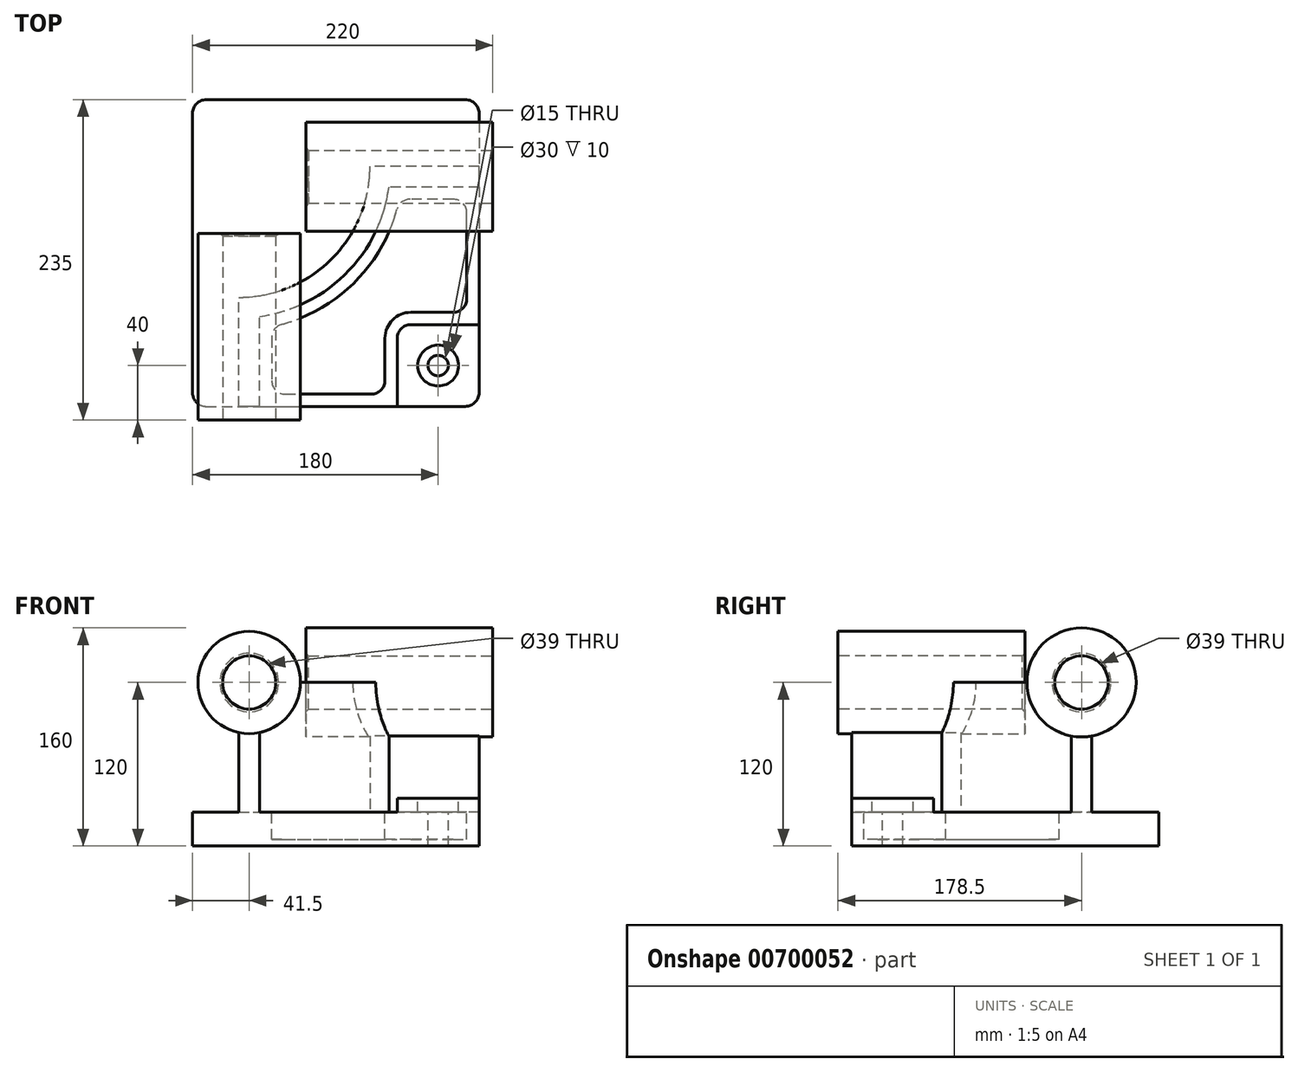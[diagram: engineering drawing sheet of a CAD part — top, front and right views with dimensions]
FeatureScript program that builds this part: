
annotation { "Feature Type Name" : "Feature", "Feature Type Description" : "" }
export const myFeature = defineFeature(function(context is Context, id is Id, definition is map)
    precondition{}
    {
        {
            var Q0;
            Q0=qCreatedBy(makeId("Top.planeOp"),FACE);
            var sketch = newSketch(context, id + "F0", { "sketchPlane" : qUnion([Q0])});
            skLineSegment(sketch, "E0.bottom", {"start": v(-105, 112.5) * mm, "end": v(105, 112.5) * mm});
            skLineSegment(sketch, "E0.top", {"start": v(-105, -112.5) * mm, "end": v(105, -112.5) * mm});
            skLineSegment(sketch, "E0.left", {"start": v(-105, 112.5) * mm, "end": v(-105, -112.5) * mm});
            skLineSegment(sketch, "E0.right", {"start": v(105, 112.5) * mm, "end": v(105, -112.5) * mm});
            skPoint(sketch, "E0.middle", {"position": v(0, 0) * mm});
            skSolve(sketch);
        }
        {
            var Q0;
            Q0=makeQuery(id+"F0.imprint","IMPRINT",FACE,{"disambiguationData":[TD([[makeQuery(id+"F0.imprint","IMPRINT",EDGE,{"derivedFrom":sQuery(id+"F0.wireOp",EDGE,"E0.bottom")}),-1.0]])]});
            extrude(context, id + "F1", {"entities" : qUnion([Q0]), "depth" : 25 * mm, "offsetDistance" : 25.4 * mm});
        }
        {
            var Q0;
            Q0=makeQuery(id+"F1.opExtrude","CAP_FACE",FACE,{"disambiguationData":[OSD([sQuery(id+"F0.wireOp",EDGE,"E0.bottom"),sQuery(id+"F0.wireOp",EDGE,"E0.top"),sQuery(id+"F0.wireOp",EDGE,"E0.left"),sQuery(id+"F0.wireOp",EDGE,"E0.right")])],"isStart":false});
            var sketch = newSketch(context, id + "F2", { "sketchPlane" : qUnion([Q0])});
            skLineSegment(sketch, "E1", {"start": v(-71, -112.5) * mm, "end": v(-71, -32.5) * mm});
            skLineSegment(sketch, "E2", {"start": v(105, 63.5) * mm, "end": v(25, 63.5) * mm});
            skArc(sketch, "E3", {"start": v(-71, -32.5) * mm, "mid": v(-3.12, -4.38) * mm, "end": v(25, 63.5) * mm});
            skLineSegment(sketch, "E4", {"start": v(-71, 63.5) * mm, "end": v(25, 63.5) * mm, "construction": true});
            skLineSegment(sketch, "E5", {"start": v(-71, 63.5) * mm, "end": v(-71, -32.5) * mm, "construction": true});
            skLineSegment(sketch, "E6.0", {"start": v(-56, -112.5) * mm, "end": v(-56, -46.48) * mm});
            skArc(sketch, "E6.1", {"start": v(-56, -46.48) * mm, "mid": v(7.49, -14.99) * mm, "end": v(38.98, 48.5) * mm});
            skLineSegment(sketch, "E6.2", {"start": v(105, 48.5) * mm, "end": v(38.98, 48.5) * mm});
            skLineSegment(sketch, "E7.0", {"start": v(105, 112.5) * mm, "end": v(105, -112.5) * mm});
            skLineSegment(sketch, "E8.0", {"start": v(-105, -112.5) * mm, "end": v(105, -112.5) * mm});
            skSolve(sketch);
        }
        {
            var Q0;
            {var subQ2=sQuery(id+"F2.wireOp",EDGE,"E1");Q0=makeQuery(id+"F2.imprint","IMPRINT",FACE,{"disambiguationData":[TD([[makeQuery(id+"F2.imprint","IMPRINT",EDGE,{"derivedFrom":subQ2}),-1.0]])]});}
            extrude(context, id + "F3", {"entities" : qUnion([Q0]), "operationType" : NewBodyOperationType.ADD, "depth" : 95 * mm, "offsetDistance" : 25.4 * mm});
        }
        {
            var Q0;
            Q0=makeQuery(id+"F3.boolean.opBoolean","MERGE",FACE,{"derivedFrom":[makeQuery(id+"F1.opExtrude","SWEPT_FACE",FACE,{"disambiguationData":[OSD([sQuery(id+"F0.wireOp",EDGE,"E0.top")])]}),makeQuery(id+"F3.opExtrude","SWEPT_FACE",FACE,{"disambiguationData":[OSD([sQuery(id+"F2.wireOp",EDGE,"E8.0")])]})]});
            var sketch = newSketch(context, id + "F4", { "sketchPlane" : qUnion([Q0])});
            skCircle(sketch, "E9", {"center": v(-63.5, 120) * mm, "radius": 37.5 * mm});
            skSolve(sketch);
        }
        {
            var Q0;
            Q0 = qSketchRegion(id + "F4", true);
            extrude(context, id + "F5", {"entities" : qUnion([Q0]), "operationType" : NewBodyOperationType.ADD, "depth" : 10 * mm, "offsetDistance" : 25.4 * mm, "hasSecondDirection" : true, "secondDirectionOppositeDirection" : true, "secondDirectionDepth" : 127 * mm});
        }
        {
            var Q0;
            Q0=makeQuery(id+"F3.boolean.opBoolean","MERGE",FACE,{"derivedFrom":[makeQuery(id+"F1.opExtrude","SWEPT_FACE",FACE,{"disambiguationData":[OSD([sQuery(id+"F0.wireOp",EDGE,"E0.right")])]}),makeQuery(id+"F3.opExtrude","SWEPT_FACE",FACE,{"disambiguationData":[OSD([sQuery(id+"F2.wireOp",EDGE,"E7.0")])]})]});
            var sketch = newSketch(context, id + "F6", { "sketchPlane" : qUnion([Q0])});
            skCircle(sketch, "E10", {"center": v(56, 120) * mm, "radius": 40 * mm});
            skSolve(sketch);
        }
        {
            var Q0;
            Q0 = qSketchRegion(id + "F6", true);
            extrude(context, id + "F7", {"entities" : qUnion([Q0]), "operationType" : NewBodyOperationType.ADD, "depth" : 10 * mm, "offsetDistance" : 25.4 * mm, "hasSecondDirection" : true, "secondDirectionOppositeDirection" : true, "secondDirectionDepth" : 127 * mm});
        }
        {
            var Q0;
            {var subQ0=sQuery(id+"F0.wireOp",EDGE,"E0.right");var subQ1=sQuery(id+"F0.wireOp",EDGE,"E0.top");Q0=makeQuery(id+"F3.boolean.opBoolean","SPLIT",FACE,{"disambiguationData":[TD([makeQuery(id+"F3.opExtrude","SWEPT_FACE",FACE,{"disambiguationData":[OSD([sQuery(id+"F2.wireOp",EDGE,"E6.0")])]})])],"derivedFrom":makeQuery(id+"F1.opExtrude","CAP_FACE",FACE,{"disambiguationData":[OSD([sQuery(id+"F0.wireOp",EDGE,"E0.bottom"),subQ1,sQuery(id+"F0.wireOp",EDGE,"E0.left"),subQ0])],"isStart":false})});}
            var sketch = newSketch(context, id + "F8", { "sketchPlane" : qUnion([Q0])});
            skLineSegment(sketch, "E11.bottom", {"start": v(105, -112.5) * mm, "end": v(45, -112.5) * mm});
            skLineSegment(sketch, "E11.top", {"start": v(105, -52.5) * mm, "end": v(45, -52.5) * mm});
            skLineSegment(sketch, "E11.left", {"start": v(105, -112.5) * mm, "end": v(105, -52.5) * mm});
            skLineSegment(sketch, "E11.right", {"start": v(45, -112.5) * mm, "end": v(45, -52.5) * mm});
            skSolve(sketch);
        }
        {
            var Q0;
            Q0 = qSketchRegion(id + "F8", true);
            extrude(context, id + "F9", {"entities" : qUnion([Q0]), "operationType" : NewBodyOperationType.ADD, "depth" : 10 * mm, "offsetDistance" : 25.4 * mm});
        }
        {
            var Q0;
            Q0=makeQuery(id+"F9.opExtrude","SWEPT_EDGE",EDGE,{"disambiguationData":[OSD([sQuery(id+"F8.wireOp",EDGE,"E11.top"),sQuery(id+"F8.wireOp",EDGE,"E11.right")])]});
            fillet(context, id + "F10", {"entities" : qUnion([Q0]), "radius" : 10 * mm, "tangentPropagation" : true, "allowEdgeOverflow" : false});
        }
        {
            var Q0;
            {var subQ0=sQuery(id+"F0.wireOp",EDGE,"E0.right");var subQ1=sQuery(id+"F0.wireOp",EDGE,"E0.top");Q0=makeQuery(id+"F3.boolean.opBoolean","SPLIT",FACE,{"disambiguationData":[TD([makeQuery(id+"F3.opExtrude","SWEPT_FACE",FACE,{"disambiguationData":[OSD([sQuery(id+"F2.wireOp",EDGE,"E6.0")])]})])],"derivedFrom":makeQuery(id+"F1.opExtrude","CAP_FACE",FACE,{"disambiguationData":[OSD([sQuery(id+"F0.wireOp",EDGE,"E0.bottom"),subQ1,sQuery(id+"F0.wireOp",EDGE,"E0.left"),subQ0])],"isStart":false})});}
            var sketch = newSketch(context, id + "F11", { "sketchPlane" : qUnion([Q0])});
            skLineSegment(sketch, "E12.0", {"start": v(-47, -54.08) * mm, "end": v(-47, -103.5) * mm});
            skArc(sketch, "E12.1", {"start": v(46.58, 39.5) * mm, "mid": v(13.85, -21.35) * mm, "end": v(-47, -54.08) * mm});
            skLineSegment(sketch, "E12.2", {"start": v(-47, -103.5) * mm, "end": v(36, -103.5) * mm});
            skLineSegment(sketch, "E12.3", {"start": v(96, 39.5) * mm, "end": v(46.58, 39.5) * mm});
            skLineSegment(sketch, "E12.4", {"start": v(36, -103.5) * mm, "end": v(36, -62.5) * mm});
            skArc(sketch, "E12.5", {"start": v(36, -62.5) * mm, "mid": v(41.56, -49.06) * mm, "end": v(55, -43.5) * mm});
            skLineSegment(sketch, "E12.6", {"start": v(55, -43.5) * mm, "end": v(96, -43.5) * mm});
            skLineSegment(sketch, "E12.7", {"start": v(96, -43.5) * mm, "end": v(96, 39.5) * mm});
            skSolve(sketch);
        }
        {
            var Q0;
            Q0=makeQuery(id+"F11.imprint","IMPRINT",FACE,{"disambiguationData":[TD([[makeQuery(id+"F11.imprint","IMPRINT",EDGE,{"derivedFrom":sQuery(id+"F11.wireOp",EDGE,"E12.0")}),1.0]])]});
            extrude(context, id + "F12", {"entities" : qUnion([Q0]), "operationType" : NewBodyOperationType.REMOVE, "oppositeDirection" : true, "depth" : 20 * mm, "offsetDistance" : 25.4 * mm});
        }
        {
            var Q0;
            Q0=makeQuery(id+"F9.opExtrude","CAP_FACE",FACE,{"disambiguationData":[OSD([sQuery(id+"F8.wireOp",EDGE,"E11.bottom"),sQuery(id+"F8.wireOp",EDGE,"E11.top"),sQuery(id+"F8.wireOp",EDGE,"E11.left"),sQuery(id+"F8.wireOp",EDGE,"E11.right")])],"isStart":false});
            var sketch = newSketch(context, id + "F13", { "sketchPlane" : qUnion([Q0])});
            skCircle(sketch, "E13", {"center": v(75, -82.5) * mm, "radius": 15 * mm});
            skSolve(sketch);
        }
        {
            var Q0;
            Q0=sQuery(id+"F13.wireOp",VERTEX,"E13.center");
            var Q1;
            Q1=makeQuery(id+"F1.opExtrude","SWEPT_BODY",BODY,{"disambiguationData":[OSD([sQuery(id+"F0.wireOp",EDGE,"E0.bottom"),sQuery(id+"F0.wireOp",EDGE,"E0.top"),sQuery(id+"F0.wireOp",EDGE,"E0.left"),sQuery(id+"F0.wireOp",EDGE,"E0.right")])]});
            hole(context, id + "F14", {"style" : HoleStyle.C_BORE, "endStyle" : HoleEndStyle.THROUGH, "holeDiameter" : 15 * mm, "cBoreDiameter" : 30 * mm, "cBoreDepth" : 10 * mm, "majorDiameter" : 6.35 * mm, "isTappedThrough" : true, "tappedDepth" : 12.7 * mm, "tapClearance" : 3, "locations" : qUnion([Q0]), "scope" : qUnion([Q1])});
        }
        {
            var Q0;
            Q0=makeQuery(id+"F12.boolean.opBoolean","COPY",EDGE,{"derivedFrom":makeQuery(id+"F12.opExtrude","SWEPT_EDGE",EDGE,{"disambiguationData":[OSD([sQuery(id+"F11.wireOp",EDGE,"E12.0"),sQuery(id+"F11.wireOp",EDGE,"E12.1")])]})});
            var Q1;
            Q1=makeQuery(id+"F12.boolean.opBoolean","COPY",EDGE,{"derivedFrom":makeQuery(id+"F12.opExtrude","SWEPT_EDGE",EDGE,{"disambiguationData":[OSD([sQuery(id+"F11.wireOp",EDGE,"E12.1"),sQuery(id+"F11.wireOp",EDGE,"E12.3")])]})});
            var Q2;
            Q2=makeQuery(id+"F12.boolean.opBoolean","COPY",EDGE,{"derivedFrom":makeQuery(id+"F12.opExtrude","SWEPT_EDGE",EDGE,{"disambiguationData":[OSD([sQuery(id+"F11.wireOp",EDGE,"E12.3"),sQuery(id+"F11.wireOp",EDGE,"E12.7")])]})});
            var Q3;
            Q3=makeQuery(id+"F12.boolean.opBoolean","COPY",EDGE,{"derivedFrom":makeQuery(id+"F12.opExtrude","SWEPT_EDGE",EDGE,{"disambiguationData":[OSD([sQuery(id+"F11.wireOp",EDGE,"E12.6"),sQuery(id+"F11.wireOp",EDGE,"E12.7")])]})});
            var Q4;
            Q4=makeQuery(id+"F12.boolean.opBoolean","COPY",EDGE,{"derivedFrom":makeQuery(id+"F12.opExtrude","SWEPT_EDGE",EDGE,{"disambiguationData":[OSD([sQuery(id+"F11.wireOp",EDGE,"E12.2"),sQuery(id+"F11.wireOp",EDGE,"E12.4")])]})});
            var Q5;
            Q5=makeQuery(id+"F12.boolean.opBoolean","COPY",EDGE,{"derivedFrom":makeQuery(id+"F12.opExtrude","SWEPT_EDGE",EDGE,{"disambiguationData":[OSD([sQuery(id+"F11.wireOp",EDGE,"E12.0"),sQuery(id+"F11.wireOp",EDGE,"E12.2")])]})});
            fillet(context, id + "F15", {"entities" : qUnion([Q0, Q1, Q2, Q3, Q4, Q5]), "radius" : 10 * mm, "tangentPropagation" : true, "allowEdgeOverflow" : false});
        }
        {
            var Q0;
            Q0=makeQuery(id+"F5.opExtrude","CAP_FACE",FACE,{"disambiguationData":[OSD([sQuery(id+"F4.wireOp",EDGE,"E9")])],"isStart":false});
            var sketch = newSketch(context, id + "F16", { "sketchPlane" : qUnion([Q0])});
            skCircle(sketch, "E14", {"center": v(-63.5, 120) * mm, "radius": 19.5 * mm});
            skSolve(sketch);
        }
        {
            var Q0;
            Q0 = qSketchRegion(id + "F16", true);
            extrude(context, id + "F17", {"entities" : qUnion([Q0]), "operationType" : NewBodyOperationType.REMOVE, "endBound" : BoundingType.THROUGH_ALL, "oppositeDirection" : true, "depth" : 25.4 * mm, "offsetDistance" : 25.4 * mm});
        }
        {
            var Q0;
            Q0=makeQuery(id+"F7.opExtrude","CAP_FACE",FACE,{"disambiguationData":[OSD([sQuery(id+"F6.wireOp",EDGE,"E10")])],"isStart":false});
            var sketch = newSketch(context, id + "F18", { "sketchPlane" : qUnion([Q0])});
            skCircle(sketch, "E15", {"center": v(56, 120) * mm, "radius": 19.5 * mm});
            skSolve(sketch);
        }
        {
            var Q0;
            Q0 = qSketchRegion(id + "F18", true);
            extrude(context, id + "F19", {"entities" : qUnion([Q0]), "operationType" : NewBodyOperationType.REMOVE, "endBound" : BoundingType.THROUGH_ALL, "oppositeDirection" : true, "depth" : 25.4 * mm, "offsetDistance" : 25.4 * mm});
        }
        {
            var Q0;
            Q0=makeQuery(id+"F17.boolean.opBoolean","COPY",EDGE,{"derivedFrom":makeQuery(id+"F17.opExtrude","CAP_EDGE",EDGE,{"disambiguationData":[OSD([sQuery(id+"F16.wireOp",EDGE,"E14")])],"isStart":true})});
            var Q1;
            Q1=makeQuery(id+"F19.boolean.opBoolean","COPY",EDGE,{"derivedFrom":makeQuery(id+"F19.opExtrude","CAP_EDGE",EDGE,{"disambiguationData":[OSD([sQuery(id+"F18.wireOp",EDGE,"E15")])],"isStart":true})});
            var Q2;
            Q2=makeQuery(id+"F19.boolean.opBoolean","INTERSECT",EDGE,{"derivedFrom":[makeQuery(id+"F7.opExtrude","CAP_FACE",FACE,{"disambiguationData":[OSD([sQuery(id+"F6.wireOp",EDGE,"E10")])],"isStart":true}),makeQuery(id+"F19.opExtrude","SWEPT_FACE",FACE,{"disambiguationData":[OSD([sQuery(id+"F18.wireOp",EDGE,"E15")])]})]});
            var Q3;
            Q3=makeQuery(id+"F17.boolean.opBoolean","INTERSECT",EDGE,{"derivedFrom":[makeQuery(id+"F5.opExtrude","CAP_FACE",FACE,{"disambiguationData":[OSD([sQuery(id+"F4.wireOp",EDGE,"E9")])],"isStart":true}),makeQuery(id+"F17.opExtrude","SWEPT_FACE",FACE,{"disambiguationData":[OSD([sQuery(id+"F16.wireOp",EDGE,"E14")])]})]});
            chamfer(context, id + "F20", {"entities" : qUnion([Q0, Q1, Q2, Q3]), "width" : 2 * mm, "tangentPropagation" : true});
        }
        {
            var Q0;
            Q0=makeQuery(id+"F1.opExtrude","SWEPT_EDGE",EDGE,{"disambiguationData":[OSD([sQuery(id+"F0.wireOp",EDGE,"E0.top"),sQuery(id+"F0.wireOp",EDGE,"E0.left")])]});
            var Q1;
            Q1=makeQuery(id+"F9.boolean.opBoolean","MERGE",EDGE,{"derivedFrom":[makeQuery(id+"F1.opExtrude","SWEPT_EDGE",EDGE,{"disambiguationData":[OSD([sQuery(id+"F0.wireOp",EDGE,"E0.top"),sQuery(id+"F0.wireOp",EDGE,"E0.right")])]}),makeQuery(id+"F9.opExtrude","SWEPT_EDGE",EDGE,{"disambiguationData":[OSD([sQuery(id+"F8.wireOp",EDGE,"E11.bottom"),sQuery(id+"F8.wireOp",EDGE,"E11.left")])]})]});
            var Q2;
            Q2=makeQuery(id+"F1.opExtrude","SWEPT_EDGE",EDGE,{"disambiguationData":[OSD([sQuery(id+"F0.wireOp",EDGE,"E0.bottom"),sQuery(id+"F0.wireOp",EDGE,"E0.right")])]});
            var Q3;
            Q3=makeQuery(id+"F1.opExtrude","SWEPT_EDGE",EDGE,{"disambiguationData":[OSD([sQuery(id+"F0.wireOp",EDGE,"E0.bottom"),sQuery(id+"F0.wireOp",EDGE,"E0.left")])]});
            fillet(context, id + "F21", {"entities" : qUnion([Q0, Q1, Q2, Q3]), "radius" : 10 * mm, "tangentPropagation" : true, "allowEdgeOverflow" : false});
        }
    });
